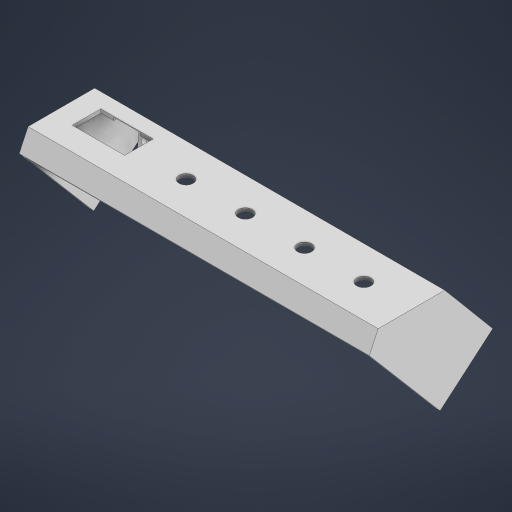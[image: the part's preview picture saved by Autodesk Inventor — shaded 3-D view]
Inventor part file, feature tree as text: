
AUTODESK INVENTOR PART (.ipt)
format: ipt  version: 2024 (Build 280153000, 153)  size: 1,152,512 bytes
history: native  units: mm
features: extrude x26, sketch x18, projected_geometry x9, other x5, chamfer x3, fillet x3, plane x2, thicken_offset x2
ambient origin geometry x8: Origin, YZ Plane, XZ Plane, XY Plane, X Axis, Y Axis, Z Axis, Center Point
bodies: Solid1 (feature_tree), Solid4 (feature_tree)
feature tree (68):
  other  "Blocks"
  sketch  "Sketch1"  dims[d0=180.0mm d1=35.0mm]
  extrude  "Extrusion1"  Depth=180.0mm
  extrude  "Extrusion2"  Depth=19.4mm
  sketch  "Sketch2"  dims[d2=7.36mm d3=19.4mm]
  extrude  "Extrusion31"  Depth=9.03mm
  extrude  "Extrusion3"  Depth=7.36mm
  extrude  "Extrusion4"  Depth=7.36mm
  extrude  "Extrusion5"  Depth=23.03mm
  chamfer  "Chamfer1"  Distance=2.0mm
  extrude  "Extrusion6"  Depth=0.4mm
  extrude  "Extrusion7"  Depth=62.0mm
  sketch  "Sketch22"  dims[d42=2.6mm d43=9.25mm d44=0.0mm d45=16.6mm d46=16.6mm d47=27.0mm d48=24.0mm d49=9.25mm d50=0.0mm d51=2.0mm d52=0.0mm d53=2.0mm d54=0.0mm d55=2.0mm d56=0.0mm d57=1.5mm d58=2.0mm d59=45.0deg d60=0.0mm d62=7.0mm d63=4.0mm d64=2.0mm d65=0.0mm d66=0.0mm d67=10.0mm d68=0.0mm d69=3.25mm d70=7.5mm d71=45.0deg d72=2.6mm d73=2.6mm d74=10.0mm d75=0.0mm d76=10.0mm d77=0.0mm d79=16.4mm d80=16.4mm d81=16.4mm d82=16.4mm d83=16.4mm d84=16.4mm d85=12.0mm d86=1.6mm d87=1.6mm d88=1.6mm d89=1.6mm d90=1.6mm d91=1.6mm d92=4.0mm d93=0.0mm d95=3.0mm d96=3.0mm d97=21.2mm d98=2.3885mm d99=45.0mm d100=9.0mm d101=3.0mm d102=1.0mm d103=0.0mm d104=13.0mm d112=2.0mm d115=13.95mm d116=0.0mm d117=10.0mm d118=6.1mm d119=0.0mm d120=10.0mm d121=1.25mm d127=52.6mm d128=1.4mm d129=2.0mm d130=4.0mm d131=0.0mm d132=5.8mm d133=0.0mm d134=5.8mm d135=0.0mm d136=6.0mm d137=6.0mm d138=10.0mm d139=0.0mm d140=5.6mm d144=2.0mm d145=4.0mm d146=4.0mm d147=2.0mm d148=19.7mm d149=3.2mm d150=5.1mm d151=3.2mm d152=5.1mm d154=4.0mm d155=0.0mm d156=1.0mm d157=0.0mm d158=3.0mm d163=0.4mm d164=0.4mm d165=0.4mm d166=0.4mm d167=4.4mm d168=0.2mm d169=0.0mm d170=4.0mm d171=6.2mm d172=0.4mm d173=16.95mm d174=0.0mm d141=0.5mm d142=0.872665mm d143=0.5mm]
  extrude  "Extrusion29"  Depth=10.0mm
  extrude  "Extrusion30"  Depth=0.4mm TaperAngle=0.0deg
  extrude  "Extrusion32"  Depth=10.0mm
  fillet  "Fillet3"  Radius=6.0mm
  plane  "Work Plane1"
  extrude  "Extrusion11"  Depth=7.0mm TaperAngle=0.0deg
  plane  "Work Plane2"
  extrude  "Extrusion12"  Depth=2.0mm
  chamfer  "Chamfer3"  Distance=9.25mm
  extrude  "Extrusion13"  Depth=0.4mm
  extrude  "Extrusion8"  Depth=0.4mm
  extrude  "Extrusion9"  Depth=0.4mm
  extrude  "Extrusion10"  Depth=0.4mm TaperAngle=0.0deg
  extrude  "Extrusion14"  Depth=2.0mm TaperAngle=0.0deg
  chamfer  "Chamfer2"  Distance=2.0mm
  extrude  "Extrusion15"  Depth=2.0mm TaperAngle=0.0deg
  sketch  "Sketch14"  dims[d28=2.0mm d29=0.4mm d30=0.0mm]
  extrude  "Extrusion16"  Depth=2.0mm TaperAngle=45.0deg
  extrude  "Extrusion21"  TaperAngle=0.0deg  [1 undecoded]
  extrude  "Extrusion24"  Depth=0.4mm
  extrude  "Extrusion25"  Depth=0.4mm
  extrude  "Extrusion26"  Depth=2.0mm TaperAngle=0.0deg
  fillet  "Fillet1"  [1 undecoded]
  extrude  "Extrusion20"  Depth=10.0mm TaperAngle=0.0deg
  fillet  "Fillet2"  Radius=3.25mm
  extrude  "Extrusion27"  Depth=0.4mm
  thicken_offset  "Thicken3"
  thicken_offset  "Thicken4"
  other  "Bottom"
  sketch  "Sketch3"  dims[d4=27.5mm d5=9.03mm]
  sketch  "Sketch4"  dims[d6=9.03mm d7=7.36mm]
  projected_geometry  "Projected Loop1"
  projected_geometry  "Projected Loop2"
  sketch  "Sketch5"  dims[d8=7.36mm d9=7.36mm]
  sketch  "Sketch6"  dims[d10=18.0mm d11=23.03mm]
  projected_geometry  "Projected Loop3"
  projected_geometry  "Projected Loop4"
  sketch  "Sketch7"  dims[d12=6.0mm]
  projected_geometry  "Projected Loop5"
  projected_geometry  "Projected Loop6"
  sketch  "Sketch8"  dims[d14=7.0mm]
  sketch  "Sketch9"  dims[d16=7.0mm]
  sketch  "Sketch10"  dims[d17=6.0mm d18=2.0mm d19=0.0mm]
  projected_geometry  "Projected Loop7"
  sketch  "Sketch11"  dims[d20=0.4mm d21=0.0mm d22=8.726646mm]
  projected_geometry  "Projected Loop8"
  projected_geometry  "Projected Loop9"
  sketch  "Sketch12"  dims[d23=6.981317mm d24=62.0mm]
  sketch  "Sketch13"  dims[d25=10.0mm d27=4.363323mm]
  other  "arduinoCover"
  sketch  "Sketch17"  dims[d31=10.0mm d32=0.0mm d33=4.0mm d34=6.0mm]
  other  "Block1"
  sketch  "Sketch19"  dims[d35=6.0mm d36=7.0mm d37=0.0mm]
  sketch  "Sketch20"  dims[d38=7.0mm d39=2.0mm d40=45.0deg d41=2.6mm]
  other  "Block1:1"
note: 2 required parameter values undecoded (feature->parameter linkage not recoverable at this tier; creation-order binding heuristic only, values carry confidence <= 0.55)
